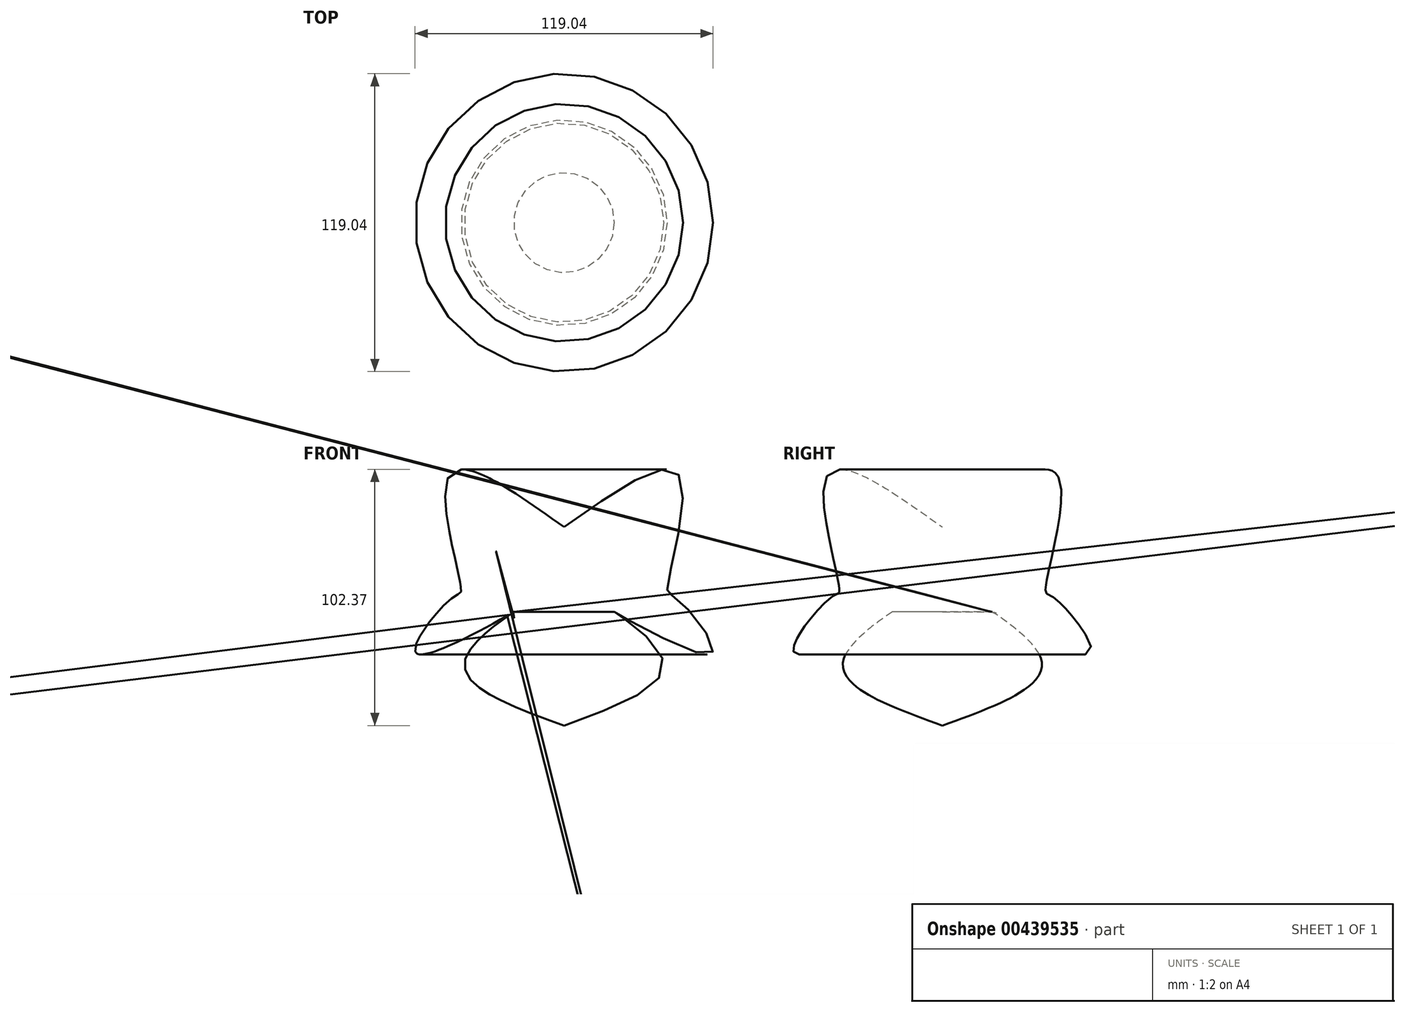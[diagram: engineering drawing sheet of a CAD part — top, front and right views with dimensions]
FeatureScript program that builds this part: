
annotation { "Feature Type Name" : "Feature", "Feature Type Description" : "" }
export const myFeature = defineFeature(function(context is Context, id is Id, definition is map)
    precondition{}
    {
        {
            var Q0;
            Q0=qCreatedBy(makeId("Front.planeOp"),FACE);
            var sketch = newSketch(context, id + "F0", { "sketchPlane" : qUnion([Q0])});
            skFitSpline(sketch, "E0", {"points": [v(0, -32.26) * mm, v(39.27, -5.16) * mm, v(20.1, 13.09) * mm, v(58.8, -3.5) * mm, v(43.88, 19.36) * mm, v(41.11, 21.57) * mm, v(46.27, 67.1) * mm, v(0, 47.01) * mm], "startDerivative": vector(372.98, 134.56) * mm, "endDerivative": vector(-346.14, -247.04) * mm});
            skLineSegment(sketch, "E1", {"start": v(0, 47.01) * mm, "end": v(0, -32.26) * mm});
            skSolve(sketch);
        }
        {
            var Q0;
            Q0=makeQuery(id+"F0.imprint","IMPRINT",FACE,{"disambiguationData":[TD([[makeQuery(id+"F0.imprint","IMPRINT",EDGE,{"derivedFrom":sQuery(id+"F0.wireOp",EDGE,"E0")}),1.0]])]});
            var Q1;
            Q1=sQuery(id+"F0.wireOp",EDGE,"E1");
            revolve(context, id + "F1", {"entities" : qUnion([Q0]), "axis" : qUnion([Q1]), "revolveType" : RevolveType.FULL});
        }
    });
